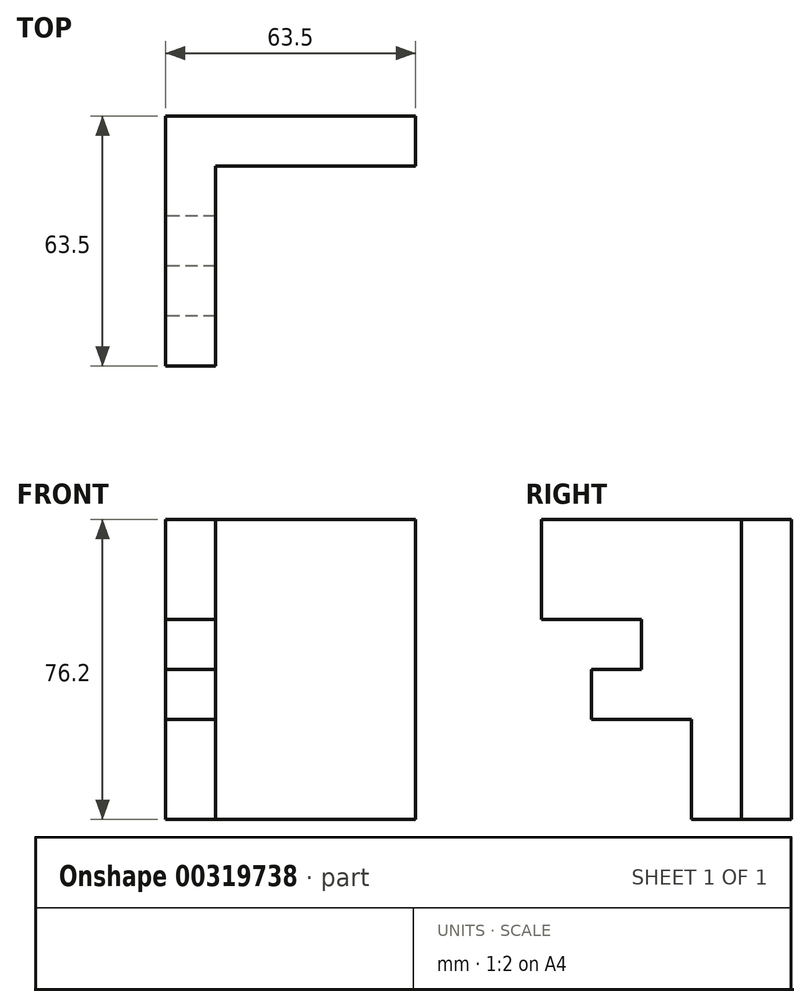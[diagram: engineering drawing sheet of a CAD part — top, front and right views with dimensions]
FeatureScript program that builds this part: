
annotation { "Feature Type Name" : "Feature", "Feature Type Description" : "" }
export const myFeature = defineFeature(function(context is Context, id is Id, definition is map)
    precondition{}
    {
        {
            var Q0;
            Q0=qCreatedBy(makeId("Right.planeOp"),FACE);
            var sketch = newSketch(context, id + "F0", { "sketchPlane" : qUnion([Q0])});
            skLineSegment(sketch, "E0", {"start": v(36.12, -44.12) * mm, "end": v(10.72, -44.12) * mm});
            skLineSegment(sketch, "E1", {"start": v(10.72, -44.12) * mm, "end": v(10.72, -18.72) * mm});
            skLineSegment(sketch, "E2", {"start": v(10.72, -18.72) * mm, "end": v(-14.68, -18.72) * mm});
            skLineSegment(sketch, "E3", {"start": v(-14.68, -18.72) * mm, "end": v(-14.68, -6.02) * mm});
            skLineSegment(sketch, "E4", {"start": v(-14.68, -6.02) * mm, "end": v(-1.98, -6.02) * mm});
            skLineSegment(sketch, "E5", {"start": v(-1.98, -6.02) * mm, "end": v(-1.98, 6.68) * mm});
            skLineSegment(sketch, "E6", {"start": v(-1.98, 6.68) * mm, "end": v(-27.38, 6.68) * mm});
            skLineSegment(sketch, "E7", {"start": v(-27.38, 6.68) * mm, "end": v(-27.38, 32.08) * mm});
            skLineSegment(sketch, "E8", {"start": v(-27.38, 32.08) * mm, "end": v(36.12, 32.08) * mm});
            skLineSegment(sketch, "E9", {"start": v(36.12, 32.08) * mm, "end": v(36.12, -44.12) * mm});
            skSolve(sketch);
        }
        {
            var Q0;
            Q0=makeQuery(id+"F0.imprint","IMPRINT",FACE,{"disambiguationData":[TD([[makeQuery(id+"F0.imprint","IMPRINT",EDGE,{"derivedFrom":sQuery(id+"F0.wireOp",EDGE,"E0")}),-1.0]])]});
            extrude(context, id + "F1", {"entities" : qUnion([Q0]), "depth" : 12.7 * mm});
        }
        {
            var Q0;
            Q0=makeQuery(id+"F1.opExtrude","CAP_FACE",FACE,{"disambiguationData":[OSD([sQuery(id+"F0.wireOp",EDGE,"E0"),sQuery(id+"F0.wireOp",EDGE,"E1"),sQuery(id+"F0.wireOp",EDGE,"E2"),sQuery(id+"F0.wireOp",EDGE,"E3"),sQuery(id+"F0.wireOp",EDGE,"E4"),sQuery(id+"F0.wireOp",EDGE,"E5"),sQuery(id+"F0.wireOp",EDGE,"E6"),sQuery(id+"F0.wireOp",EDGE,"E7"),sQuery(id+"F0.wireOp",EDGE,"E8"),sQuery(id+"F0.wireOp",EDGE,"E9")])],"isStart":false});
            var sketch = newSketch(context, id + "F2", { "sketchPlane" : qUnion([Q0])});
            skLineSegment(sketch, "E10", {"start": v(23.42, -44.12) * mm, "end": v(23.42, 32.08) * mm});
            skLineSegment(sketch, "E11", {"start": v(23.42, 32.08) * mm, "end": v(36.12, 32.08) * mm});
            skLineSegment(sketch, "E12", {"start": v(36.12, 32.08) * mm, "end": v(36.12, -44.12) * mm});
            skLineSegment(sketch, "E13", {"start": v(36.12, -44.12) * mm, "end": v(23.42, -44.12) * mm});
            skSolve(sketch);
        }
        {
            var Q0;
            Q0 = qSketchRegion(id + "F2", true);
            extrude(context, id + "F3", {"entities" : qUnion([Q0]), "operationType" : NewBodyOperationType.ADD, "depth" : 50.8 * mm});
        }
    });
